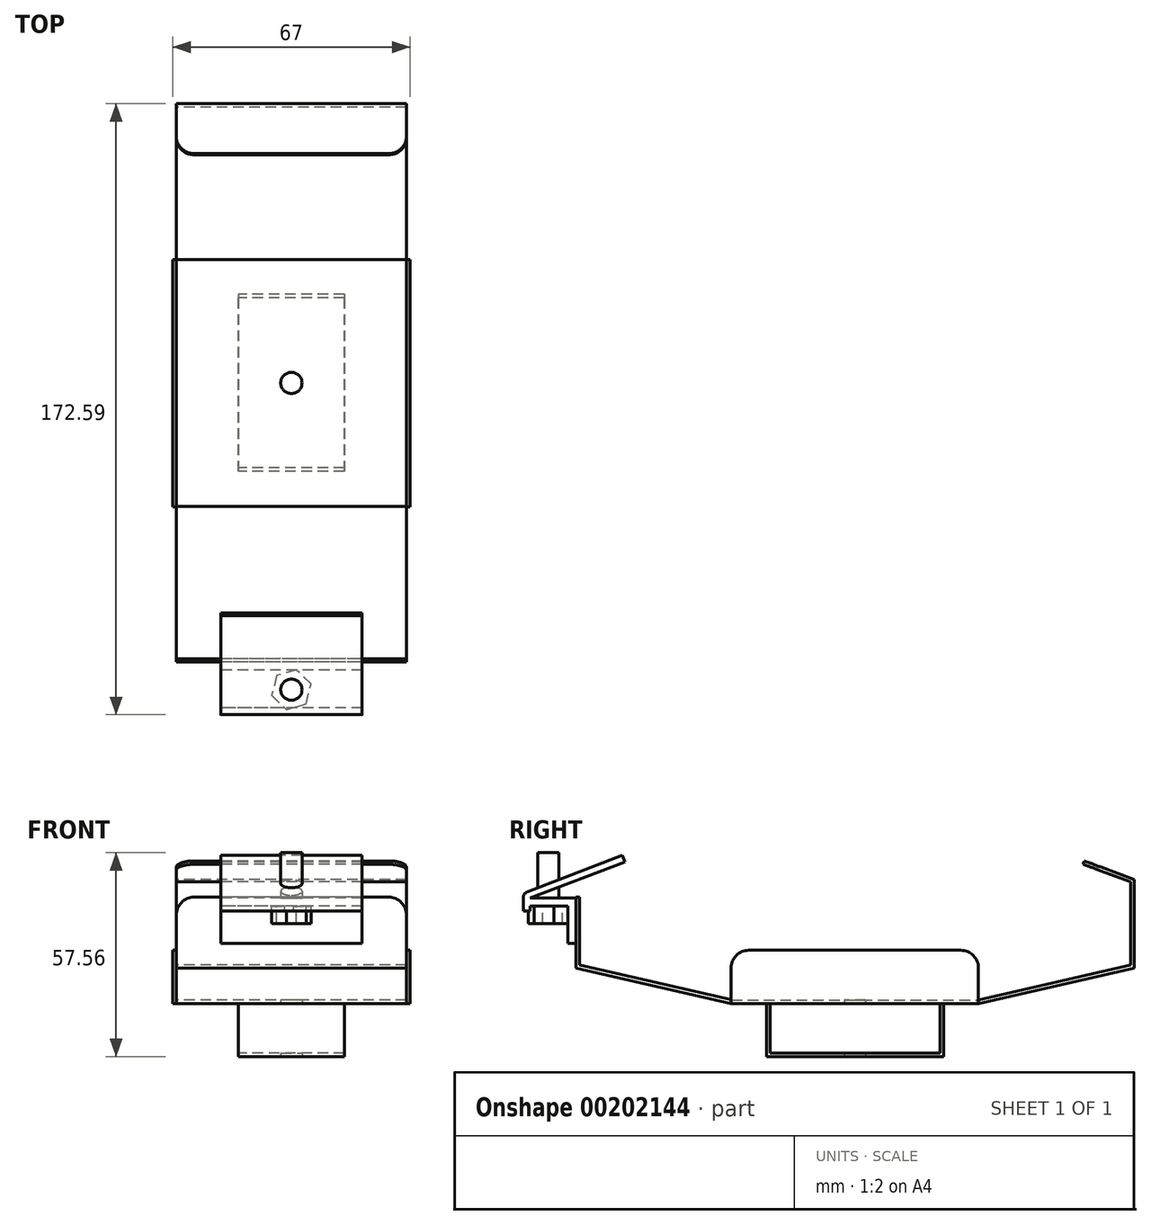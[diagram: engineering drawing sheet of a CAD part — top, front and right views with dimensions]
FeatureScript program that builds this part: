
annotation { "Feature Type Name" : "Feature", "Feature Type Description" : "" }
export const myFeature = defineFeature(function(context is Context, id is Id, definition is map)
    precondition{}
    {
        {
            var Q0;
            Q0=qCreatedBy(makeId("Right.planeOp"),FACE);
            var sketch = newSketch(context, id + "F0", { "sketchPlane" : qUnion([Q0])});
            skLineSegment(sketch, "E0", {"start": v(-35, 0) * mm, "end": v(35, 0) * mm});
            skLineSegment(sketch, "E1", {"start": v(35, 0) * mm, "end": v(78.87, 10) * mm});
            skLineSegment(sketch, "E2", {"start": v(78.87, 10) * mm, "end": v(78.87, 35) * mm});
            skLineSegment(sketch, "E3", {"start": v(78.87, 35) * mm, "end": v(64.82, 40.24) * mm});
            skLineSegment(sketch, "E4", {"start": v(-35, 0) * mm, "end": v(-78.87, 10) * mm});
            skLineSegment(sketch, "E5", {"start": v(-78.87, 10) * mm, "end": v(-78.87, 30) * mm});
            skLineSegment(sketch, "E6", {"start": v(0, 76.2) * mm, "end": v(0, -66.06) * mm, "construction": true});
            skLineSegment(sketch, "E7.0", {"start": v(-77.87, 10.8) * mm, "end": v(-77.87, 30) * mm});
            skLineSegment(sketch, "E7.1", {"start": v(-34.89, 1) * mm, "end": v(-77.87, 10.8) * mm});
            skLineSegment(sketch, "E7.2", {"start": v(77.87, 34.3) * mm, "end": v(64.47, 39.3) * mm});
            skLineSegment(sketch, "E7.3", {"start": v(77.87, 10.8) * mm, "end": v(77.87, 34.3) * mm});
            skLineSegment(sketch, "E7.4", {"start": v(34.89, 1) * mm, "end": v(77.87, 10.8) * mm});
            skLineSegment(sketch, "E7.5", {"start": v(-34.89, 1) * mm, "end": v(34.89, 1) * mm});
            skLineSegment(sketch, "E8", {"start": v(-78.87, 30) * mm, "end": v(-77.87, 30) * mm});
            skLineSegment(sketch, "E9", {"start": v(64.47, 39.3) * mm, "end": v(64.82, 40.24) * mm});
            skSolve(sketch);
        }
        {
            var Q0;
            Q0 = qSketchRegion(id + "F0", true);
            extrude(context, id + "F1", {"entities" : qUnion([Q0]), "endBound" : BoundingType.SYMMETRIC, "depth" : 65 * mm});
        }
        {
            var Q0;
            Q0=makeQuery(id+"F1.opExtrude","CAP_FACE",FACE,{"disambiguationData":[OSD([sQuery(id+"F0.wireOp",EDGE,"E0"),sQuery(id+"F0.wireOp",EDGE,"E1"),sQuery(id+"F0.wireOp",EDGE,"E2"),sQuery(id+"F0.wireOp",EDGE,"E3"),sQuery(id+"F0.wireOp",EDGE,"E4"),sQuery(id+"F0.wireOp",EDGE,"E5"),sQuery(id+"F0.wireOp",EDGE,"E7.0"),sQuery(id+"F0.wireOp",EDGE,"E7.1"),sQuery(id+"F0.wireOp",EDGE,"E7.2"),sQuery(id+"F0.wireOp",EDGE,"E7.3"),sQuery(id+"F0.wireOp",EDGE,"E7.4"),sQuery(id+"F0.wireOp",EDGE,"E7.5"),sQuery(id+"F0.wireOp",EDGE,"E8"),sQuery(id+"F0.wireOp",EDGE,"E9")])],"isStart":false});
            var sketch = newSketch(context, id + "F2", { "sketchPlane" : qUnion([Q0])});
            skLineSegment(sketch, "E10.bottom", {"start": v(-35, 0) * mm, "end": v(34.89, 0) * mm});
            skLineSegment(sketch, "E10.top", {"start": v(-35, 15) * mm, "end": v(34.89, 15) * mm});
            skLineSegment(sketch, "E10.left", {"start": v(-35, 0) * mm, "end": v(-35, 15) * mm});
            skLineSegment(sketch, "E10.right", {"start": v(34.89, 0) * mm, "end": v(34.89, 15) * mm});
            skSolve(sketch);
        }
        {
            var Q0;
            Q0 = qSketchRegion(id + "F2", true);
            extrude(context, id + "F3", {"entities" : qUnion([Q0]), "depth" : 1 * mm});
        }
        {
            var Q0;
            Q0=makeQuery(id+"F3.opExtrude","SWEPT_BODY",BODY,{"disambiguationData":[OSD([sQuery(id+"F2.wireOp",EDGE,"E10.bottom"),sQuery(id+"F2.wireOp",EDGE,"E10.top"),sQuery(id+"F2.wireOp",EDGE,"E10.left"),sQuery(id+"F2.wireOp",EDGE,"E10.right")])]});
            var Q1;
            Q1=qCreatedBy(makeId("Right.planeOp"),FACE);
            mirror(context, id + "F4", {"operationType" : NewBodyOperationType.ADD, "entities" : qUnion([Q0]), "mirrorPlane" : qUnion([Q1])});
        }
        {
            var Q0;
            Q0=qCreatedBy(makeId("Right.planeOp"),FACE);
            var sketch = newSketch(context, id + "F5", { "sketchPlane" : qUnion([Q0])});
            skLineSegment(sketch, "E11", {"start": v(-91.72, 29.74) * mm, "end": v(-65, 40) * mm});
            skLineSegment(sketch, "E12", {"start": v(-65, 40) * mm, "end": v(-65.72, 41.87) * mm});
            skLineSegment(sketch, "E13", {"start": v(-65.72, 41.87) * mm, "end": v(-92.44, 31.6) * mm});
            skLineSegment(sketch, "E14", {"start": v(0, 69.98) * mm, "end": v(0, -56.2) * mm, "construction": true});
            skLineSegment(sketch, "E15.0", {"start": v(77.87, 34.3) * mm, "end": v(64.47, 39.3) * mm, "construction": true});
            skLineSegment(sketch, "E16.0", {"start": v(77.87, 10.8) * mm, "end": v(77.87, 34.3) * mm, "construction": true});
            skLineSegment(sketch, "E17.0.0", {"start": v(34.89, 1) * mm, "end": v(34.89, 0) * mm, "construction": true});
            skLineSegment(sketch, "E17.0.1", {"start": v(34.89, 0) * mm, "end": v(35, 0) * mm, "construction": true});
            skLineSegment(sketch, "E17.0.2", {"start": v(35, 0) * mm, "end": v(78.87, 10) * mm, "construction": true});
            skLineSegment(sketch, "E17.0.3", {"start": v(78.87, 10) * mm, "end": v(78.87, 35) * mm, "construction": true});
            skLineSegment(sketch, "E17.0.4", {"start": v(78.87, 35) * mm, "end": v(64.82, 40.24) * mm, "construction": true});
            skLineSegment(sketch, "E17.0.5", {"start": v(64.82, 40.24) * mm, "end": v(64.47, 39.3) * mm, "construction": true});
            skLineSegment(sketch, "E17.0.6", {"start": v(64.47, 39.3) * mm, "end": v(77.87, 34.3) * mm, "construction": true});
            skLineSegment(sketch, "E17.0.7", {"start": v(77.87, 34.3) * mm, "end": v(77.87, 10.8) * mm, "construction": true});
            skLineSegment(sketch, "E17.0.8", {"start": v(77.87, 10.8) * mm, "end": v(34.89, 1) * mm, "construction": true});
            skLineSegment(sketch, "E18", {"start": v(-91.72, 29.74) * mm, "end": v(-91.72, 26.1) * mm});
            skLineSegment(sketch, "E19", {"start": v(-91.72, 26.1) * mm, "end": v(-93.72, 26.1) * mm});
            skLineSegment(sketch, "E20", {"start": v(-93.72, 26.1) * mm, "end": v(-93.72, 29.74) * mm});
            skPoint(sketch, "E21.visualSharp", {"position": v(-93.72, 31.12) * mm});
            skArc(sketch, "E21.filletArc", {"start": v(-92.44, 31.6) * mm, "mid": v(-93.37, 30.87) * mm, "end": v(-93.72, 29.74) * mm});
            skSolve(sketch);
        }
        {
            var Q0;
            Q0 = qSketchRegion(id + "F5", true);
            extrude(context, id + "F6", {"entities" : qUnion([Q0]), "endBound" : BoundingType.SYMMETRIC, "depth" : 40 * mm});
        }
        {
            var Q0;
            Q0=qCreatedBy(makeId("Right.planeOp"),FACE);
            var sketch = newSketch(context, id + "F7", { "sketchPlane" : qUnion([Q0])});
            skLineSegment(sketch, "E22", {"start": v(-91.72, 29.74) * mm, "end": v(-78.87, 29.74) * mm});
            skLineSegment(sketch, "E23", {"start": v(-78.87, 29.74) * mm, "end": v(-78.87, 16.9) * mm});
            skLineSegment(sketch, "E24", {"start": v(-78.87, 16.9) * mm, "end": v(-81.06, 16.9) * mm});
            skLineSegment(sketch, "E25", {"start": v(-81.06, 16.9) * mm, "end": v(-81.06, 27.56) * mm});
            skLineSegment(sketch, "E26", {"start": v(-81.06, 27.56) * mm, "end": v(-91.72, 27.56) * mm});
            skLineSegment(sketch, "E27", {"start": v(-91.72, 27.56) * mm, "end": v(-91.72, 29.74) * mm});
            skSolve(sketch);
        }
        {
            var Q0;
            Q0 = qSketchRegion(id + "F7", true);
            extrude(context, id + "F8", {"entities" : qUnion([Q0]), "endBound" : BoundingType.SYMMETRIC, "depth" : 40 * mm});
        }
        {
            var Q0;
            Q0=makeQuery(id+"F8.opExtrude","SWEPT_FACE",FACE,{"disambiguationData":[OSD([sQuery(id+"F7.wireOp",EDGE,"E26")])]});
            var sketch = newSketch(context, id + "F9", { "sketchPlane" : qUnion([Q0])});
            skCircle(sketch, "E28", {"center": v(0, 86.66) * mm, "radius": 3 * mm});
            skPoint(sketch, "E28.centerSnap0", {"position": v(0, 81.06) * mm});
            skSolve(sketch);
        }
        {
            var Q0;
            Q0 = qSketchRegion(id + "F9", true);
            var Q1;
            Q1=makeQuery(id+"F6.opExtrude","SWEPT_FACE",FACE,{"disambiguationData":[OSD([sQuery(id+"F5.wireOp",EDGE,"E13")])]});
            extrude(context, id + "F10", {"entities" : qUnion([Q0]), "operationType" : NewBodyOperationType.REMOVE, "endBound" : BoundingType.UP_TO_SURFACE, "oppositeDirection" : true, "endBoundEntityFace" : qUnion([Q1]), "depth" : 25 * mm});
        }
        {
            var Q0;
            Q0=makeQuery(id+"F8.opExtrude","SWEPT_FACE",FACE,{"disambiguationData":[OSD([sQuery(id+"F7.wireOp",EDGE,"E26")])]});
            var sketch = newSketch(context, id + "F11", { "sketchPlane" : qUnion([Q0])});
            skCircle(sketch, "E29", {"center": v(0, 86.66) * mm, "radius": 3 * mm});
            skSolve(sketch);
        }
        {
            var Q0;
            Q0 = qSketchRegion(id + "F11", true);
            extrude(context, id + "F12", {"entities" : qUnion([Q0]), "oppositeDirection" : true, "depth" : 15 * mm});
        }
        {
            var Q0;
            Q0=makeQuery(id+"F12.opExtrude","CAP_FACE",FACE,{"disambiguationData":[OSD([sQuery(id+"F11.wireOp",EDGE,"E29")])],"isStart":true});
            var sketch = newSketch(context, id + "F13", { "sketchPlane" : qUnion([Q0])});
            skCircle(sketch, "E30.cCircle", {"center": v(0, 86.66) * mm, "radius": 5 * mm, "construction": true});
            skLineSegment(sketch, "E30.0", {"start": v(-4.16, 82.66) * mm, "end": v(-5.55, 88.26) * mm});
            skLineSegment(sketch, "E30.1", {"start": v(-5.55, 88.26) * mm, "end": v(-1.4, 92.27) * mm});
            skLineSegment(sketch, "E30.2", {"start": v(-1.4, 92.27) * mm, "end": v(4.16, 90.67) * mm});
            skLineSegment(sketch, "E30.3", {"start": v(4.16, 90.67) * mm, "end": v(5.55, 85.07) * mm});
            skLineSegment(sketch, "E30.4", {"start": v(5.55, 85.07) * mm, "end": v(1.4, 81.06) * mm});
            skLineSegment(sketch, "E30.5", {"start": v(1.4, 81.06) * mm, "end": v(-4.16, 82.66) * mm});
            skPoint(sketch, "E30.0.midPoint", {"position": v(-4.85, 85.46) * mm});
            skSolve(sketch);
        }
        {
            var Q0;
            Q0 = qSketchRegion(id + "F13", true);
            extrude(context, id + "F14", {"entities" : qUnion([Q0]), "operationType" : NewBodyOperationType.ADD, "depth" : 5 * mm});
        }
        {
            var Q0;
            Q0=makeQuery(id+"F3.opExtrude","SWEPT_EDGE",EDGE,{"disambiguationData":[OSD([sQuery(id+"F2.wireOp",EDGE,"E10.top"),sQuery(id+"F2.wireOp",EDGE,"E10.right")])]});
            var Q1;
            Q1=makeQuery(id+"F3.opExtrude","SWEPT_EDGE",EDGE,{"disambiguationData":[OSD([sQuery(id+"F2.wireOp",EDGE,"E10.top"),sQuery(id+"F2.wireOp",EDGE,"E10.left")])]});
            var Q2;
            Q2=makeQuery(id+"F1.opExtrude","CAP_EDGE",EDGE,{"disambiguationData":[OSD([sQuery(id+"F0.wireOp",EDGE,"E8")])],"isStart":false});
            var Q3;
            Q3=makeQuery(id+"F1.opExtrude","CAP_EDGE",EDGE,{"disambiguationData":[OSD([sQuery(id+"F0.wireOp",EDGE,"E9")])],"isStart":false});
            var Q4;
            Q4=makeQuery(id+"F1.opExtrude","CAP_EDGE",EDGE,{"disambiguationData":[OSD([sQuery(id+"F0.wireOp",EDGE,"E8")])],"isStart":true});
            var Q5;
            Q5=makeQuery(id+"F4.opPattern","COPY",EDGE,{"derivedFrom":makeQuery(id+"F3.opExtrude","SWEPT_EDGE",EDGE,{"disambiguationData":[OSD([sQuery(id+"F2.wireOp",EDGE,"E10.top"),sQuery(id+"F2.wireOp",EDGE,"E10.left")])]}),"instanceName":"1"});
            var Q6;
            Q6=makeQuery(id+"F4.opPattern","COPY",EDGE,{"derivedFrom":makeQuery(id+"F3.opExtrude","SWEPT_EDGE",EDGE,{"disambiguationData":[OSD([sQuery(id+"F2.wireOp",EDGE,"E10.top"),sQuery(id+"F2.wireOp",EDGE,"E10.right")])]}),"instanceName":"1"});
            var Q7;
            Q7=makeQuery(id+"F1.opExtrude","CAP_EDGE",EDGE,{"disambiguationData":[OSD([sQuery(id+"F0.wireOp",EDGE,"E9")])],"isStart":true});
            fillet(context, id + "F15", {"entities" : qUnion([Q0, Q1, Q2, Q3, Q4, Q5, Q6, Q7]), "radius" : 5 * mm, "tangentPropagation" : true, "allowEdgeOverflow" : false});
        }
        {
            var Q0;
            Q0=qCreatedBy(makeId("Right.planeOp"),FACE);
            var sketch = newSketch(context, id + "F16", { "sketchPlane" : qUnion([Q0])});
            skLineSegment(sketch, "E31", {"start": v(-25, 0) * mm, "end": v(-25, -15) * mm});
            skLineSegment(sketch, "E32", {"start": v(-25, -15) * mm, "end": v(25, -15) * mm});
            skLineSegment(sketch, "E33", {"start": v(25, -15) * mm, "end": v(25, 0) * mm});
            skLineSegment(sketch, "E34", {"start": v(25, 0) * mm, "end": v(24, 0) * mm});
            skLineSegment(sketch, "E35", {"start": v(24, 0) * mm, "end": v(24, -14) * mm});
            skLineSegment(sketch, "E36", {"start": v(24, -14) * mm, "end": v(-24, -14) * mm});
            skLineSegment(sketch, "E37", {"start": v(-24, -14) * mm, "end": v(-24, 0) * mm});
            skLineSegment(sketch, "E38", {"start": v(-24, 0) * mm, "end": v(-25, 0) * mm});
            skSolve(sketch);
        }
        {
            var Q0;
            Q0 = qSketchRegion(id + "F16", true);
            extrude(context, id + "F17", {"entities" : qUnion([Q0]), "endBound" : BoundingType.SYMMETRIC, "depth" : 30 * mm});
        }
        {
            var Q0;
            Q0=makeQuery(id+"F17.opExtrude","SWEPT_FACE",FACE,{"disambiguationData":[OSD([sQuery(id+"F16.wireOp",EDGE,"E32")])]});
            var sketch = newSketch(context, id + "F18", { "sketchPlane" : qUnion([Q0])});
            skCircle(sketch, "E39", {"center": v(0, 0) * mm, "radius": 3 * mm});
            skSolve(sketch);
        }
        {
            var Q0;
            Q0 = qSketchRegion(id + "F18", true);
            extrude(context, id + "F19", {"entities" : qUnion([Q0]), "operationType" : NewBodyOperationType.REMOVE, "endBound" : BoundingType.THROUGH_ALL, "oppositeDirection" : true, "depth" : 25 * mm});
        }
    });
